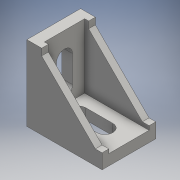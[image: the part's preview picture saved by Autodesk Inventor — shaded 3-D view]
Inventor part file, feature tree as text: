
AUTODESK INVENTOR PART (.ipt)
format: ipt  version: 2016 (Build 200138000, 138)  size: 208,384 bytes
history: native  units: mm
features: extrude x8, sketch x8, projected_geometry x8
ambient origin geometry x8: Origin, YZ Plane, XZ Plane, XY Plane, X Axis, Y Axis, Z Axis, Center Point
bodies: Solid1 (feature_tree)
feature tree (24):
  extrude  "Extrusion1"  Depth=28.0mm
  extrude  "Extrusion2"  Depth=10.0mm
  extrude  "Extrusion3"  Depth=6.0mm
  extrude  "Extrusion4"  Depth=4.0mm
  extrude  "Extrusion5"  Depth=10.0mm
  extrude  "Extrusion6"  Depth=6.0mm
  extrude  "Extrusion7"  Depth=1.0mm
  extrude  "Extrusion8"  Depth=1.0mm
  sketch  "Sketch1"  dims[d0=20.0mm d1=28.0mm]
  sketch  "Sketch2"  dims[d2=4.0mm d3=0.0mm d4=10.0mm]
  projected_geometry  "Projected Loop1"
  sketch  "Sketch3"  dims[d5=6.0mm d6=9.0mm]
  projected_geometry  "Projected Loop2"
  sketch  "Sketch4"  dims[d7=30.0mm d8=0.0mm d9=4.0mm]
  projected_geometry  "Projected Loop3"
  sketch  "Sketch5"  dims[d10=24.0mm d11=0.0mm d12=10.0mm]
  projected_geometry  "Projected Loop4"
  sketch  "Sketch6"  dims[d13=6.0mm d14=9.0mm]
  projected_geometry  "Projected Loop5"
  sketch  "Sketch7"  dims[d15=24.0mm d16=0.0mm d17=1.0mm]
  projected_geometry  "Projected Loop6"
  sketch  "Sketch8"  dims[d18=5.8mm d19=1.0mm d20=1.0mm d21=0.0mm d22=1.0mm d23=5.8mm d24=1.0mm d25=1.0mm d26=0.0mm d27=1.5mm d28=2.5mm d29=1.5mm d30=2.5mm d31=2.5mm d32=0.0mm d33=2.5mm d34=0.0mm]
  projected_geometry  "Projected Loop7"
  projected_geometry  "Projected Loop8"
